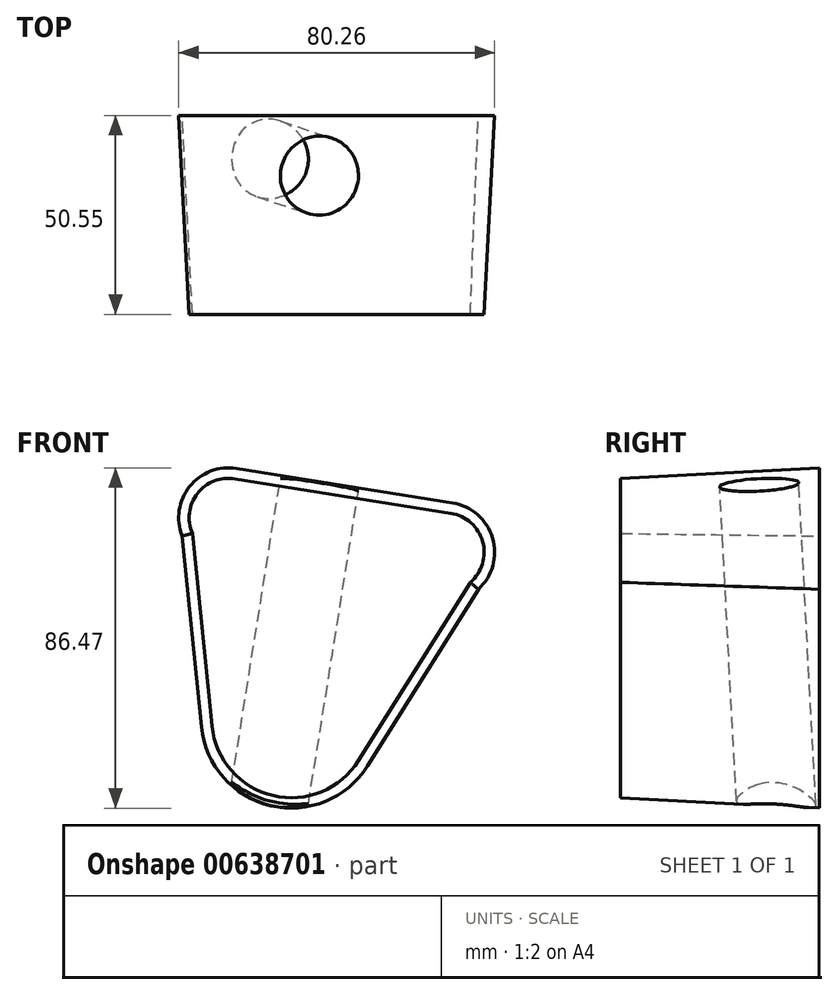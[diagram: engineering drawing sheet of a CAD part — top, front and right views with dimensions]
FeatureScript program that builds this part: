
annotation { "Feature Type Name" : "Feature", "Feature Type Description" : "" }
export const myFeature = defineFeature(function(context is Context, id is Id, definition is map)
    precondition{}
    {
        {
            var Q0;
            Q0=qCreatedBy(makeId("Front.planeOp"),FACE);
            var sketch = newSketch(context, id + "F0", { "sketchPlane" : qUnion([Q0])});
            skCircle(sketch, "E0", {"center": v(-34.17, 39.14) * mm, "radius": 12.7 * mm});
            skCircle(sketch, "E1", {"center": v(20.69, 30.37) * mm, "radius": 12.7 * mm});
            skCircle(sketch, "E2", {"center": v(-18.3, -11.77) * mm, "radius": 22.86 * mm});
            skLineSegment(sketch, "E3", {"start": v(-46, 34.51) * mm, "end": v(-41.03, -14.15) * mm});
            skLineSegment(sketch, "E4", {"start": v(-32.17, 51.68) * mm, "end": v(22.7, 42.91) * mm});
            skLineSegment(sketch, "E5", {"start": v(32.86, 26.73) * mm, "end": v(1.07, -23.92) * mm});
            skSolve(sketch);
        }
        {
            var Q0;
            Q0 = qSketchRegion(id + "F0", true);
            extrude(context, id + "F1", {"entities" : qUnion([Q0]), "depth" : 50.55 * mm, "offsetDistance" : 25.4 * mm, "hasDraft" : true, "draftAngle" : 3 * degree, "draftPullDirection" : true});
        }
        {
            var Q0;
            Q0=makeQuery(id+"F1.opExtrude","SWEPT_FACE",FACE,{"disambiguationData":[OSD([sQuery(id+"F0.wireOp",EDGE,"E4")])]});
            var sketch = newSketch(context, id + "F2", { "sketchPlane" : qUnion([Q0])});
            skCircle(sketch, "E6", {"center": v(-18.59, -12.78) * mm, "radius": 10.05 * mm});
            skSolve(sketch);
        }
        {
            var Q0;
            Q0=makeQuery(id+"F2.imprint","IMPRINT",FACE,{"disambiguationData":[TD([[makeQuery(id+"F2.imprint","IMPRINT",EDGE,{"derivedFrom":sQuery(id+"F2.wireOp",EDGE,"E6")}),1.0]])]});
            extrude(context, id + "F3", {"entities" : qUnion([Q0]), "operationType" : NewBodyOperationType.REMOVE, "endBound" : BoundingType.THROUGH_ALL, "oppositeDirection" : true, "depth" : 25.4 * mm, "offsetDistance" : 25.4 * mm});
        }
    });
